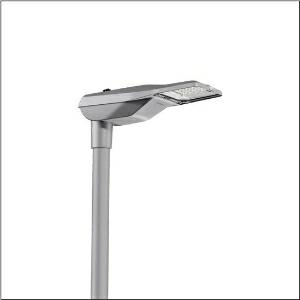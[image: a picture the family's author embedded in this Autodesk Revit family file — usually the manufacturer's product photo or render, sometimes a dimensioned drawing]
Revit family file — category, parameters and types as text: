
# Revit family: streetlight_sl_21_micro___st0_8a_5xe1c43s08db_42f9
name_source: partatom
category: Lighting Fixtures
units: mm (PartAtom-declared; Revit-internal decimal feet)

## family parameters
Cut with Voids When Loaded = No
Host = Face
Light Source = No
Part Type = Normal
Room Calculation Point = No
Round Connector Dimension = Use Diameter
Shared = No

## types (1)
- --- (1 x LED, 5320 lm, 39.1 W, 4000K)
    Apparent Load = 39 VA
    CIE Flux Codes = 38 75 97 100 100
    Color Rendering = 70
    Color Temperature = 4000K
    Default Elevation = 1800 mm
    Description = Streetlight SL 21 micro, mast luminaire, primary light control with lens, of PMMA, primary optical cover: cover, of toughened safety glass, transparent, light distribution: ST0.8a, light emission: direct distribution, primary light characteristic: asymmetric, installation type: side-entry, post-top, LED, High Power LED, rated luminous flux: 5.320lm, luminous efficacy: 136lm/W, light colour: 740, colour temperature: 4000K, control gear: D4i, control: flexible luminous flux parameterisation, time-dependent luminous flux control, constant luminous flux control, overheat protection, pre-setting: logarithmic dimming characteristic, mains connection: 220..240V, AC, 50/60Hz, start of lifetime: 39W, end of service life: 41W, reduction: 18W, luminaire housing, of diecast aluminium, powder-coated, Siteco® metallic grey (DB 702S), corrosivity category C5 mid according to DIN EN ISO 12944, please order mast flange separately, inclination adjustable: 0°, 5°, 10°, 15°, sealing non-destructively replaceable, multi-level sealing system, length: 528mm, width: 235mm, height: 110mm, mast flange for spigot size: 42mm (side-entry): 5XC10008XM4, 60/48mm (side-entry/post-top): 5XC10108XM2, 76/60mm (side-entry/post-top): 5XC10108XM1, Smart Interface above, protection rating (complete): IP66, insulation class (complete): insulation class II (safety insulation), certification: CE, ENEC, ENEC+, VDE, impact resistance: IK10, permissible operating ambient temperature for outdoor applications: -40..+50°C, standard-compliant lighting for roads and squares, packaging unit: 1 piece

Light Distribution: ST0.8a
    Height = 110 mm
    Lamp = 1 x LED
    Lamp Light Flux = 5320 lm
    Lamp Power = 39.1 W
    Lamp count = 1
    Length = 528 mm
    Luminous efficacy = 136 lm/W
    Manufacturer = Siteco
    ModVariant = No
    Model = 5XE1C43S08DB
    Number of Poles = 1
    OnlyDefault = Yes
    Power Factor = 1
    Product Name = Streetlight SL 21 micro | ST0.8a
    Product group = mast luminaire | pylon top
    ProductGroupID = 6100
    Protection Class = Protection class II
    Protection Degree = IP 66
    RLX_Detail_Level = 1
    RLX_Emergency_Light_Flux = 0 lm
    RLX_Emergency_Type = 0
    RLX_Emergency_Type_DB = No
    RlxData = <blob elided: 99181 chars, md5=7d827d75>
    Socket = socket
    Standby Power = 0 W
    System Light Flux = 5320 lm
    System Power = 39 W
    Type Comments = factory setting: luminous flux: 100 % | dim-lin: 254 | 765 mA
    Type Image = l_1277292.jpg
    URL = http://relux.com
    VarID = @adj_154428
    Voltage = 0 V
    Weight = 0.00 kg
    Width = 235 mm

## geometry (parser evidence)
native form markers: Blend x4, Sweep x9
no freeform markers — native parametric forms only
